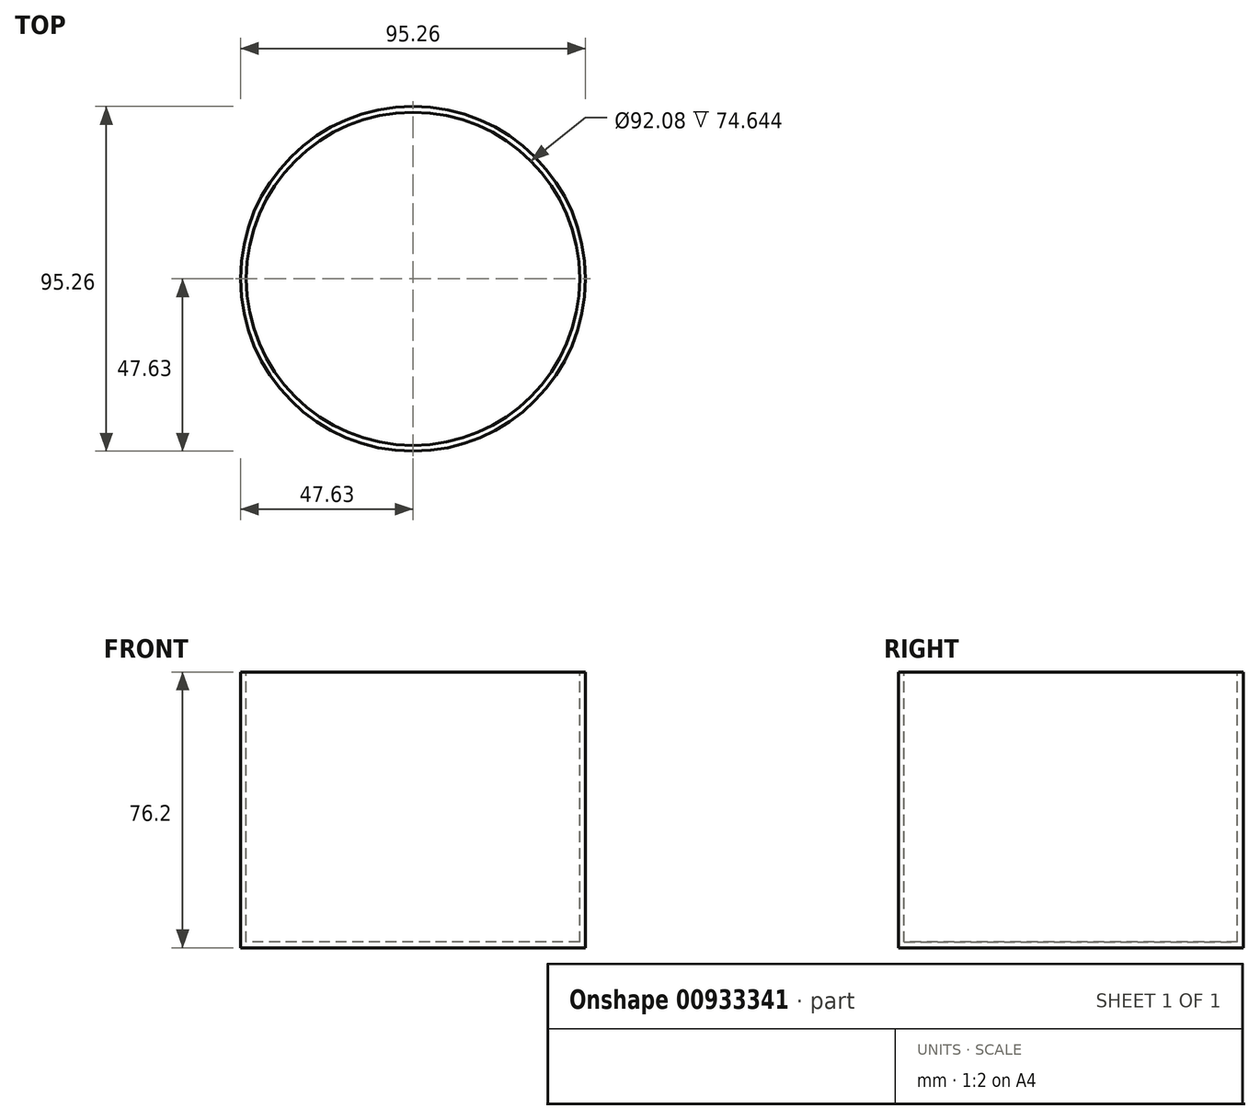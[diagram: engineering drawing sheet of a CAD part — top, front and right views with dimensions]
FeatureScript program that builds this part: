
annotation { "Feature Type Name" : "Feature", "Feature Type Description" : "" }
export const myFeature = defineFeature(function(context is Context, id is Id, definition is map)
    precondition{}
    {
        {
            var Q0;
            Q0=qCreatedBy(makeId("Top.planeOp"),FACE);
            var sketch = newSketch(context, id + "F0", { "sketchPlane" : qUnion([Q0])});
            skCircle(sketch, "E0", {"center": v(0, 0) * mm, "radius": 47.63 * mm});
            skSolve(sketch);
        }
        {
            var Q0;
            Q0 = qSketchRegion(id + "F0", true);
            extrude(context, id + "F1", {"entities" : qUnion([Q0]), "depth" : 76.2 * mm, "offsetDistance" : 25.4 * mm});
        }
        {
            var Q0;
            Q0=makeQuery(id+"F1.opExtrude","CAP_FACE",FACE,{"disambiguationData":[OSD([sQuery(id+"F0.wireOp",EDGE,"E0")])],"isStart":false});
            var sketch = newSketch(context, id + "F2", { "sketchPlane" : qUnion([Q0])});
            skCircle(sketch, "E1", {"center": v(0, 0) * mm, "radius": 46.04 * mm});
            skSolve(sketch);
        }
        {
            var Q0;
            Q0 = qSketchRegion(id + "F2", true);
            var Q1;
            Q1=makeQuery(id+"F1.opExtrude","CAP_FACE",FACE,{"disambiguationData":[OSD([sQuery(id+"F0.wireOp",EDGE,"E0")])],"isStart":true});
            extrude(context, id + "F3", {"entities" : qUnion([Q0]), "operationType" : NewBodyOperationType.REMOVE, "endBound" : BoundingType.UP_TO_SURFACE, "oppositeDirection" : true, "depth" : 73.02 * mm, "endBoundEntityFace" : qUnion([Q1]), "hasOffset" : true, "offsetDistance" : 1.56 * mm});
        }
    });
